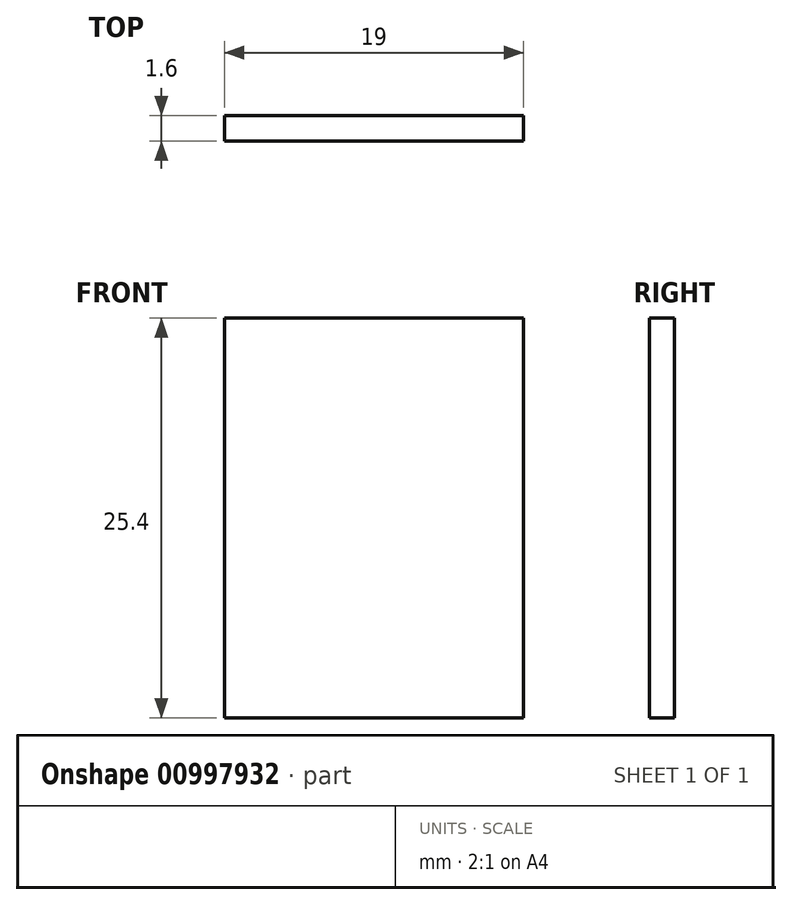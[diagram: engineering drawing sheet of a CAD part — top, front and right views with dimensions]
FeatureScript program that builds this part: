
annotation { "Feature Type Name" : "Feature", "Feature Type Description" : "" }
export const myFeature = defineFeature(function(context is Context, id is Id, definition is map)
    precondition{}
    {
        {
            var Q0;
            Q0=qCreatedBy(makeId("Front.planeOp"),FACE);
            var sketch = newSketch(context, id + "F0", { "sketchPlane" : qUnion([Q0])});
            skLineSegment(sketch, "E0.bottom", {"start": v(9.5, -12.7) * mm, "end": v(-9.5, -12.7) * mm});
            skLineSegment(sketch, "E0.top", {"start": v(9.5, 12.7) * mm, "end": v(-9.5, 12.7) * mm});
            skLineSegment(sketch, "E0.left", {"start": v(9.5, -12.7) * mm, "end": v(9.5, 12.7) * mm});
            skLineSegment(sketch, "E0.right", {"start": v(-9.5, -12.7) * mm, "end": v(-9.5, 12.7) * mm});
            skPoint(sketch, "E0.middle", {"position": v(0, 0) * mm});
            skSolve(sketch);
        }
        {
            var Q0;
            Q0=makeQuery(id+"F0.imprint","IMPRINT",FACE,{"disambiguationData":[TD([[makeQuery(id+"F0.imprint","IMPRINT",EDGE,{"derivedFrom":sQuery(id+"F0.wireOp",EDGE,"E0.bottom")}),-1.0]])]});
            extrude(context, id + "F1", {"entities" : qUnion([Q0]), "depth" : 1.6 * mm, "offsetDistance" : 25 * mm});
        }
    });
